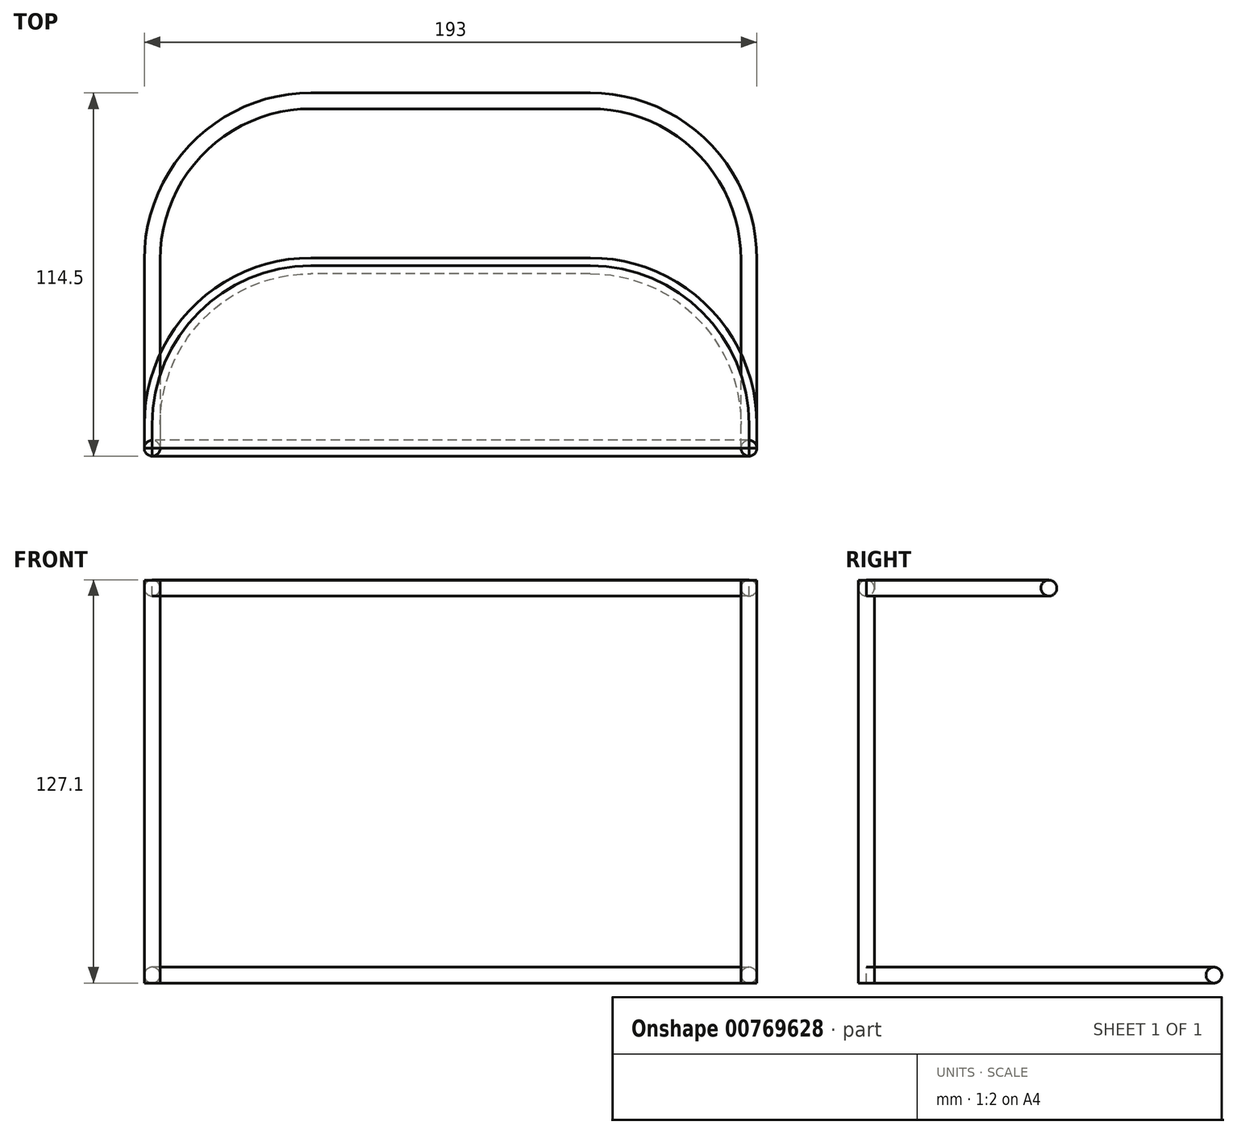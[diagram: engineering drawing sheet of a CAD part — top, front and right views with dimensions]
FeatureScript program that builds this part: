
annotation { "Feature Type Name" : "Feature", "Feature Type Description" : "" }
export const myFeature = defineFeature(function(context is Context, id is Id, definition is map)
    precondition{}
    {
        {
            var Q0;
            Q0=qCreatedBy(makeId("Top.planeOp"),FACE);
            var sketch = newSketch(context, id + "F0", { "sketchPlane" : qUnion([Q0])});
            skLineSegment(sketch, "E0", {"start": v(-94, 0) * mm, "end": v(94, 0) * mm, "construction": true});
            skCircle(sketch, "E1", {"center": v(-94, 0) * mm, "radius": 2.5 * mm});
            skCircle(sketch, "E2", {"center": v(94, 0) * mm, "radius": 2.5 * mm});
            skSolve(sketch);
        }
        {
            var Q0;
            Q0=makeQuery(id+"F0.imprint","IMPRINT",FACE,{"disambiguationData":[TD([[makeQuery(id+"F0.imprint","IMPRINT",EDGE,{"derivedFrom":sQuery(id+"F0.wireOp",EDGE,"E2")}),1.0]])]});
            var Q1;
            Q1=makeQuery(id+"F0.imprint","IMPRINT",FACE,{"disambiguationData":[TD([[makeQuery(id+"F0.imprint","IMPRINT",EDGE,{"derivedFrom":sQuery(id+"F0.wireOp",EDGE,"E1")}),1.0]])]});
            extrude(context, id + "F1", {"entities" : qUnion([Q0, Q1]), "depth" : 127 * mm});
        }
        {
            var Q0;
            Q0=qCreatedBy(makeId("Top.planeOp"),FACE);
            cPlane(context, id + "F2", {"entities" : qUnion([Q0]), "cplaneType" : CPlaneType.OFFSET, "offset" : 124.5 * mm, "width" : 150 * mm, "height" : 150 * mm});
        }
        {
            var Q0;
            Q0=qCreatedBy(id+"F2.planeOp",FACE);
            var sketch = newSketch(context, id + "F3", { "sketchPlane" : qUnion([Q0])});
            skCircle(sketch, "E3.0", {"center": v(-94, 0) * mm, "radius": 2.5 * mm});
            skCircle(sketch, "E4.0", {"center": v(94, 0) * mm, "radius": 2.5 * mm});
            skLineSegment(sketch, "E5", {"start": v(-94, 0) * mm, "end": v(94, 0) * mm});
            skSolve(sketch);
        }
        {
            var Q0;
            Q0=qCreatedBy(makeId("Right.planeOp"),FACE);
            cPlane(context, id + "F4", {"entities" : qUnion([Q0]), "cplaneType" : CPlaneType.OFFSET, "offset" : (188 / 2) * mm, "width" : 150 * mm, "height" : 150 * mm});
        }
        {
            var Q0;
            Q0=qCreatedBy(id+"F4.planeOp",FACE);
            var sketch = newSketch(context, id + "F5", { "sketchPlane" : qUnion([Q0])});
            skPoint(sketch, "E6.0", {"position": v(0, 124.5) * mm});
            skCircle(sketch, "E7", {"center": v(0, 124.5) * mm, "radius": 2.5 * mm});
            skSolve(sketch);
        }
        {
            var Q0;
            Q0=makeQuery(id+"F5.imprint","IMPRINT",FACE,{"disambiguationData":[TD([[makeQuery(id+"F5.imprint","IMPRINT",EDGE,{"derivedFrom":sQuery(id+"F5.wireOp",EDGE,"E7")}),1.0]])]});
            var Q1;
            Q1=sQuery(id+"F5.wireOp",EDGE,"E7");
            var Q2;
            Q2=sQuery(id+"F3.wireOp",EDGE,"E5");
            var Q3;
            Q3=sQuery(id+"F3.wireOp",EDGE,"E5");
            sweep(context, id + "F6", {"profiles" : qUnion([Q0]), "surfaceProfiles" : qUnion([Q1, Q2]), "path" : qUnion([Q3])});
        }
        {
            var Q0;
            Q0=qCreatedBy(makeId("Front.planeOp"),FACE);
            var sketch = newSketch(context, id + "F7", { "sketchPlane" : qUnion([Q0])});
            skCircle(sketch, "E8", {"center": v(94, 2.5) * mm, "radius": 2.5 * mm});
            skSolve(sketch);
        }
        {
            var Q0;
            Q0=qCreatedBy(makeId("Top.planeOp"),FACE);
            var sketch = newSketch(context, id + "F8", { "sketchPlane" : qUnion([Q0])});
            skLineSegment(sketch, "E9", {"start": v(94, 0) * mm, "end": v(94, 59.5) * mm});
            skLineSegment(sketch, "E10", {"start": v(44, 109.5) * mm, "end": v(-44, 109.5) * mm});
            skLineSegment(sketch, "E11", {"start": v(-94, 59.5) * mm, "end": v(-94, 0) * mm});
            skPoint(sketch, "E12.visualSharp", {"position": v(-94, 109.5) * mm});
            skArc(sketch, "E12.filletArc", {"start": v(-44, 109.5) * mm, "mid": v(-79.36, 94.86) * mm, "end": v(-94, 59.5) * mm});
            skPoint(sketch, "E13.visualSharp", {"position": v(94, 109.5) * mm});
            skArc(sketch, "E13.filletArc", {"start": v(94, 59.5) * mm, "mid": v(79.36, 94.86) * mm, "end": v(44, 109.5) * mm});
            skSolve(sketch);
        }
        {
            var Q0;
            Q0=makeQuery(id+"F7.imprint","IMPRINT",FACE,{"disambiguationData":[TD([[makeQuery(id+"F7.imprint","IMPRINT",EDGE,{"derivedFrom":sQuery(id+"F7.wireOp",EDGE,"E8")}),1.0]])]});
            var Q1;
            Q1=sQuery(id+"F8.wireOp",EDGE,"E9");
            var Q2;
            Q2=sQuery(id+"F8.wireOp",EDGE,"E13.filletArc");
            var Q3;
            Q3=sQuery(id+"F8.wireOp",EDGE,"E10");
            var Q4;
            Q4=sQuery(id+"F8.wireOp",EDGE,"E12.filletArc");
            var Q5;
            Q5=sQuery(id+"F8.wireOp",EDGE,"E11");
            sweep(context, id + "F9", {"profiles" : qUnion([Q0]), "path" : qUnion([Q1, Q2, Q3, Q4, Q5])});
        }
        {
            var Q0;
            Q0=qCreatedBy(id+"F2.planeOp",FACE);
            var sketch = newSketch(context, id + "F10", { "sketchPlane" : qUnion([Q0])});
            skLineSegment(sketch, "E14", {"start": v(94, 0) * mm, "end": v(94, 7.5) * mm});
            skLineSegment(sketch, "E15", {"start": v(44, 57.5) * mm, "end": v(-44, 57.5) * mm});
            skLineSegment(sketch, "E16", {"start": v(-94, 7.5) * mm, "end": v(-94, 0) * mm});
            skPoint(sketch, "E17.visualSharp", {"position": v(-94, 57.5) * mm});
            skArc(sketch, "E17.filletArc", {"start": v(-44, 57.5) * mm, "mid": v(-79.36, 42.86) * mm, "end": v(-94, 7.5) * mm});
            skPoint(sketch, "E18.visualSharp", {"position": v(94, 57.5) * mm});
            skArc(sketch, "E18.filletArc", {"start": v(94, 7.5) * mm, "mid": v(79.36, 42.86) * mm, "end": v(44, 57.5) * mm});
            skSolve(sketch);
        }
        {
            var Q0;
            Q0=qCreatedBy(makeId("Front.planeOp"),FACE);
            var sketch = newSketch(context, id + "F11", { "sketchPlane" : qUnion([Q0])});
            skPoint(sketch, "E19.0", {"position": v(94, 124.5) * mm});
            skCircle(sketch, "E20", {"center": v(94, 124.5) * mm, "radius": 2.5 * mm});
            skSolve(sketch);
        }
        {
            var Q0;
            Q0=makeQuery(id+"F11.imprint","IMPRINT",FACE,{"disambiguationData":[TD([[makeQuery(id+"F11.imprint","IMPRINT",EDGE,{"derivedFrom":sQuery(id+"F11.wireOp",EDGE,"E20")}),1.0]])]});
            var Q1;
            Q1=sQuery(id+"F10.wireOp",EDGE,"E14");
            var Q2;
            Q2=sQuery(id+"F10.wireOp",EDGE,"E18.filletArc");
            var Q3;
            Q3=sQuery(id+"F10.wireOp",EDGE,"E15");
            var Q4;
            Q4=sQuery(id+"F10.wireOp",EDGE,"E17.filletArc");
            var Q5;
            Q5=sQuery(id+"F10.wireOp",EDGE,"E16");
            sweep(context, id + "F12", {"profiles" : qUnion([Q0]), "path" : qUnion([Q1, Q2, Q3, Q4, Q5])});
        }
        {
            var Q0;
            Q0=qCreatedBy(id+"F2.planeOp",FACE);
            var sketch = newSketch(context, id + "F13", { "sketchPlane" : qUnion([Q0])});
            skArc(sketch, "E21", {"start": v(-44, 60) * mm, "mid": v(-81.12, 44.62) * mm, "end": v(-96.5, 7.5) * mm});
            skLineSegment(sketch, "E22", {"start": v(-96.5, 0) * mm, "end": v(-96.5, 7.5) * mm});
            skLineSegment(sketch, "E23", {"start": v(-44, 60) * mm, "end": v(44, 60) * mm});
            skArc(sketch, "E24", {"start": v(96.5, 7.5) * mm, "mid": v(81.12, 44.62) * mm, "end": v(44, 60) * mm});
            skLineSegment(sketch, "E25", {"start": v(96.5, 7.5) * mm, "end": v(96.5, 0) * mm});
            skSolve(sketch);
        }
        {
            var Q0;
            Q0=qCreatedBy(makeId("Top.planeOp"),FACE);
            cPlane(context, id + "F14", {"entities" : qUnion([Q0]), "cplaneType" : CPlaneType.OFFSET, "offset" : 2.5 * mm, "width" : 150 * mm, "height" : 150 * mm});
        }
        {
            var Q0;
            Q0=qCreatedBy(id+"F14.planeOp",FACE);
            var sketch = newSketch(context, id + "F15", { "sketchPlane" : qUnion([Q0])});
            skArc(sketch, "E26", {"start": v(-44, 112) * mm, "mid": v(-81.12, 96.62) * mm, "end": v(-96.5, 59.5) * mm});
            skLineSegment(sketch, "E27", {"start": v(-44, 112) * mm, "end": v(44, 112) * mm});
            skArc(sketch, "E28", {"start": v(96.5, 59.5) * mm, "mid": v(81.12, 96.62) * mm, "end": v(44, 112) * mm});
            skLineSegment(sketch, "E29", {"start": v(96.5, 59.5) * mm, "end": v(96.5, 0) * mm});
            skLineSegment(sketch, "E30", {"start": v(-96.5, 0) * mm, "end": v(-96.5, 59.5) * mm});
            skSolve(sketch);
        }
        {
            var Q0;
            Q0=qCreatedBy(makeId("Right.planeOp"),FACE);
            var sketch = newSketch(context, id + "F16", { "sketchPlane" : qUnion([Q0])});
            skPoint(sketch, "E31.0", {"position": v(60, 124.5) * mm});
            skPoint(sketch, "E32.0", {"position": v(112, 2.5) * mm});
            skFitSpline(sketch, "E33", {"points": [v(60, 124.5) * mm, v(112, 2.5) * mm], "startDerivative": vector(40.52, -242.4) * mm, "endDerivative": vector(1.83, -10.83) * mm});
            skSolve(sketch);
        }
        {
            var Q0;
            Q0=qSketchRegion(id+"F13",true);
            var Q1;
            Q1=qSketchRegion(id+"F15",true);
            var Q2;
            Q2=qConstructionFilter(qBodyType(qCreatedBy(id+"F13",EDGE),BodyType.WIRE),ConstructionObject.NO);
            var Q3;
            Q3=qConstructionFilter(qBodyType(qCreatedBy(id+"F15",EDGE),BodyType.WIRE),ConstructionObject.NO);
            var Q4;
            Q4=qConstructionFilter(qBodyType(qCreatedBy(id+"F16",EDGE),BodyType.WIRE),ConstructionObject.NO);
            loft(context, id + "F17", {"bodyType" : ToolBodyType.SURFACE, "addGuides" : true, "sheetProfilesArray" : [{ "sheetProfileEntities" : qUnion([Q0]) }, { "sheetProfileEntities" : qUnion([Q1]) }], "wireProfilesArray" : [{ "wireProfileEntities" : qUnion([Q2]) }, { "wireProfileEntities" : qUnion([Q3]) }], "guidesArray" : [{ "guideEntities" : qUnion([Q4]), "guideDerivativeType" : LoftGuideDerivativeType.DEFAULT, "guideDerivativeMagnitude" : 1 }]});
        }
        {
            var Q0;
            Q0=qCreatedBy(id+"F2.planeOp",FACE);
            cPlane(context, id + "F18", {"entities" : qUnion([Q0]), "cplaneType" : CPlaneType.OFFSET, "offset" : 2.5 * mm, "width" : 150 * mm, "height" : 150 * mm});
        }
        {
            var Q0;
            Q0=qCreatedBy(id+"F18.planeOp",FACE);
            var sketch = newSketch(context, id + "F19", { "sketchPlane" : qUnion([Q0])});
            skLineSegment(sketch, "E34.0", {"start": v(-94, 0) * mm, "end": v(94, 0) * mm});
            skPoint(sketch, "E35.0", {"position": v(94, 0) * mm});
            skLineSegment(sketch, "E36.0", {"start": v(94, 0) * mm, "end": v(94, 7.5) * mm});
            skLineSegment(sketch, "E37.0", {"start": v(-94, 7.5) * mm, "end": v(-94, 0) * mm});
            skLineSegment(sketch, "E38", {"start": v(44, 57.5) * mm, "end": v(-44, 57.5) * mm});
            skArc(sketch, "E39", {"start": v(-44, 57.5) * mm, "mid": v(-79.36, 42.86) * mm, "end": v(-94, 7.5) * mm});
            skArc(sketch, "E40", {"start": v(94, 7.5) * mm, "mid": v(79.36, 42.86) * mm, "end": v(44, 57.5) * mm});
            skPoint(sketch, "E41.orphan", {"position": v(-94, 59.5) * mm});
            skPoint(sketch, "E42.orphan", {"position": v(94, 59.5) * mm});
            skSolve(sketch);
        }
        {
            var Q0;
            Q0=qSketchRegion(id+"F19",true);
            var Q1;
            Q1=qConstructionFilter(qBodyType(qCreatedBy(id+"F19",EDGE),BodyType.WIRE),ConstructionObject.NO);
            extrude(context, id + "F20", {"entities" : qUnion([Q0]), "surfaceEntities" : qUnion([Q1]), "depth" : 0.1 * mm});
        }
    });
